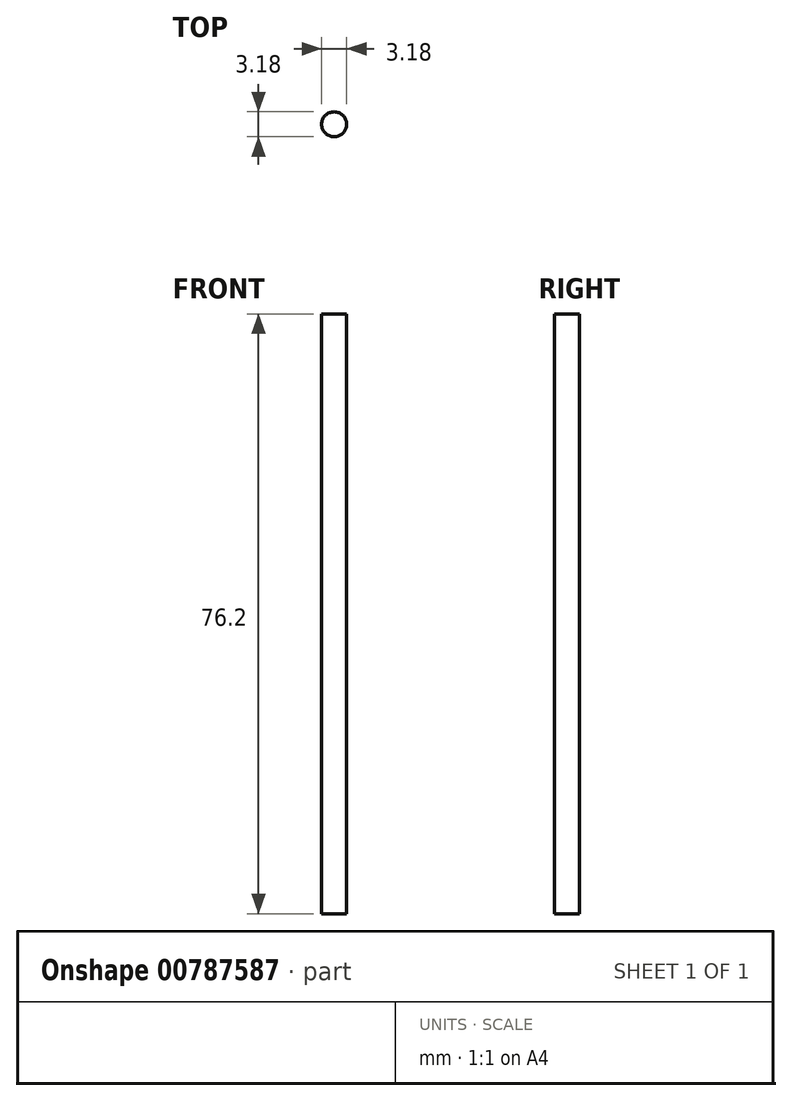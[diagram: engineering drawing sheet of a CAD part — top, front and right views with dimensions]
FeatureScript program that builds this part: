
annotation { "Feature Type Name" : "Feature", "Feature Type Description" : "" }
export const myFeature = defineFeature(function(context is Context, id is Id, definition is map)
    precondition{}
    {
        {
            var Q0;
            Q0=qCreatedBy(makeId("Top.planeOp"),FACE);
            var sketch = newSketch(context, id + "F0", { "sketchPlane" : qUnion([Q0])});
            skCircle(sketch, "E0", {"center": v(0, 0) * mm, "radius": 1.59 * mm});
            skSolve(sketch);
        }
        {
            var Q0;
            Q0=makeQuery(id+"F0.imprint","IMPRINT",FACE,{"disambiguationData":[TD([[makeQuery(id+"F0.imprint","IMPRINT",EDGE,{"derivedFrom":sQuery(id+"F0.wireOp",EDGE,"E0")}),1.0]])]});
            extrude(context, id + "F1", {"entities" : qUnion([Q0]), "depth" : 76.2 * mm, "offsetDistance" : 25.4 * mm});
        }
    });
